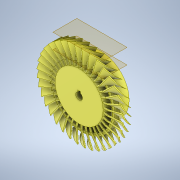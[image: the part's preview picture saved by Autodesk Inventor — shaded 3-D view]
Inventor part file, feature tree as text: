
AUTODESK INVENTOR PART (.ipt)
format: ipt  version: 2021.2 (Build 252289000, 289)  size: 4,591,616 bytes
history: native  units: in
note: dims shown in document units (in); Inventor stores cm internally (conversion verified against a paired STEP export)
features: sketch x6, extrude x4, plane x2, loft x1, pattern_circular x1, revolve x1, other x1
ambient origin geometry x8: Origin, YZ Plane, XZ Plane, XY Plane, X Axis, Y Axis, Z Axis, Center Point
bodies: Solid1 (feature_tree)
feature tree (16):
  extrude  "Extrusion1"  Depth=1.0in
  plane  "Work Plane1"
  extrude  "Extrusion2"  Depth=0.0312in
  plane  "Work Plane2"
  loft  "Loft1"
  pattern_circular  "Circular Pattern1"  Count=36 Angle=360.0deg
  revolve  "Revolution1"  [1 undecoded]
  extrude  "Extrusion3"  Depth=0.05in
  extrude  "Extrusion4"  Depth=0.5in
  sketch  "Sketch1"  dims[d0=2.2in d1=1.0in d2=0.0777in]
  sketch  "Sketch2"  dims[d3=1.3in d4=0.0312in]
  sketch  "Sketch3"  dims[d5=0.5in d6=0.0in d7=2.0in]
  other  "Edges1"
  sketch  "Sketch4"  dims[d8=0.0in d9=90.0deg]
  sketch  "Sketch5"  dims[d10=0.0in d11=90.0deg d12=14.1732in d13=360.0deg]
  sketch  "Sketch6"  dims[d15=0.125in d16=0.3in d17=0.05in d18=0.5in d20=0.6in d21=90.0deg d22=0.315in d23=0.125in d24=0.125in d25=0.0in d26=0.0in d27=3.9375in d28=0.0in d29=0.0in]
note: 1 required parameter value undecoded (feature->parameter linkage not recoverable at this tier; creation-order binding heuristic only, values carry confidence <= 0.55)
